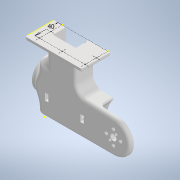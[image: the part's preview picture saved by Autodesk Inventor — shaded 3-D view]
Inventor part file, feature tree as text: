
AUTODESK INVENTOR PART (.ipt)
format: ipt  version: 2020 (Build 240168000, 168)  size: 836,608 bytes
history: native  units: mm
features: sketch x26, fillet x22, extrude x16, hole x7, other x6, reference x4, shell x1, projected_geometry x1
ambient origin geometry x8: Origin, YZ Plane, XZ Plane, XY Plane, X Axis, Y Axis, Z Axis, Center Point
bodies: Solid1 (feature_tree)
feature tree (83):
  extrude  "Extrusion1"  Depth=58.0mm
  shell  "Shell1"  Thickness=15.0mm
  extrude  "Extrusion2"  Depth=30.0mm
  extrude  "Extrusion3"  Depth=120.0mm
  hole  "Hole1"  [1 undecoded]
  extrude  "Extrusion5"  Depth=60.0mm
  hole  "Hole2"  [1 undecoded]
  extrude  "Extrusion6"  Depth=40.0mm
  extrude  "Extrusion7"  TaperAngle=0.0deg  [1 undecoded]
  extrude  "Extrusion8"  Depth=3.4mm
  fillet  "Fillet1"  Radius=6.3mm
  fillet  "Fillet2"  [1 undecoded]
  fillet  "Fillet4"  Radius=20.0mm
  fillet  "Fillet5"  Radius=81.0mm
  fillet  "Fillet7"  [1 undecoded]
  fillet  "Fillet10"  [1 undecoded]
  fillet  "Fillet11"  Radius=25.0mm
  fillet  "Fillet13"  Radius=3.4mm
  extrude  "Extrusion9"  TaperAngle=90.0deg  [1 undecoded]
  hole  "Hole3"  [1 undecoded]
  fillet  "Fillet15"  [1 undecoded]
  fillet  "Fillet16"  [1 undecoded]
  extrude  "Extrusion12"  Depth=90.0mm
  extrude  "Extrusion13"  Depth=12.0mm
  extrude  "Extrusion14"  Depth=24.0mm TaperAngle=0.0deg
  fillet  "Fillet17"  Radius=2.0mm
  fillet  "Fillet18"  Radius=18.0mm
  fillet  "Fillet19"  Radius=10.0mm
  fillet  "Fillet21"  Radius=18.0mm
  extrude  "Extrusion15"  Depth=4.0mm
  fillet  "Fillet24"  Radius=4.0mm
  fillet  "Fillet25"  Radius=7.0mm
  fillet  "Fillet26"  Radius=12.0mm
  fillet  "Fillet27"  Radius=5.5mm
  hole  "Hole6"  [1 undecoded]
  hole  "Hole7"  [1 undecoded]
  fillet  "Fillet28"  Radius=25.0mm
  sketch  "Sketch29"  dims[d114=5.0mm d115=3.0mm d116=0.0mm d117=25.0mm]
  extrude  "Extrusion16"  Depth=20.0mm TaperAngle=0.0deg
  hole  "Hole8"  [1 undecoded]
  extrude  "Extrusion17"  Depth=12.0mm
  extrude  "Extrusion18"  Depth=3.0mm
  hole  "Hole10"  [1 undecoded]
  extrude  "Extrusion19"  Depth=6.0mm TaperAngle=0.0deg
  fillet  "Fillet29"  Radius=10.0mm
  fillet  "Fillet30"  Radius=3.0mm
  sketch  "Sketch38"  dims[d146=3.0mm]
  sketch  "Sketch39"  dims[d147=3.4mm d148=15.875mm d149=11.0mm d150=2.6mm d151=90.0deg d152=8.0mm d153=0.0mm d154=40.0mm d155=3.4mm d156=15.875mm d157=6.3mm d158=2.6mm d159=90.0deg d160=8.0mm d161=0.0mm d162=3.0mm d163=4.0mm d164=2.0mm d165=0.0mm d166=2.4mm d167=5.0mm d168=4.4mm d169=2.0mm d170=90.0deg d171=5.0mm d172=20.594885mm d173=7.0mm d174=105.185mm d175=0.0mm d183=7.0mm d184=2.0mm d185=0.0mm d186=2.4mm d187=5.0mm d188=4.4mm d189=2.0mm d190=90.0deg d191=5.0mm d192=20.594885mm d193=4.0mm d194=4.5mm d195=0.0mm d196=5.0mm d197=4.0mm d199=7.0mm d200=7.0mm d216=5.0mm]
  fillet  "Fillet38"  Radius=3.0mm
  sketch  "Sketch1"  dims[d4=54.0mm d6=58.0mm d7=15.0mm]
  sketch  "Sketch3"  dims[d8=65.0mm d9=30.0mm]
  sketch  "Sketch4"  dims[d10=0.0mm d12=120.0mm]
  sketch  "Sketch5"  dims[d14=15.0mm d15=80.0mm]
  sketch  "Sketch7"  dims[d16=52.0mm d17=60.0mm]
  sketch  "Sketch8"  dims[d19=24.0mm d20=0.0mm]
  sketch  "Sketch9"  dims[d21=7.0mm d22=40.0mm]
  sketch  "Sketch10"  dims[d23=20.0mm d24=0.0mm]
  sketch  "Sketch11"  dims[d25=25.0mm d26=3.4mm d27=6.0mm d28=6.3mm d29=2.0mm d30=90.0deg d31=20.0mm d32=0.0mm d46=81.0mm d47=0.0mm d48=0.0mm d49=25.0mm d50=3.4mm d51=6.0mm]
  sketch  "Sketch13"  dims[d52=6.3mm d53=2.0mm d54=90.0deg]
  sketch  "Sketch16"  dims[d55=20.0mm d56=0.0mm d57=11.0mm d58=0.0mm d59=0.0mm]
  sketch  "Sketch20"  dims[d60=81.0mm d61=90.0mm]
  sketch  "Sketch22"  dims[d62=24.0mm d63=0.0mm d64=12.0mm]
  sketch  "Sketch23"  dims[d65=6.0mm d66=24.0mm d67=0.0mm d68=2.0mm d69=18.0mm d71=10.0mm d72=18.0mm]
  sketch  "Sketch24"  dims[d74=8.0mm d77=4.0mm d78=4.0mm d80=7.0mm d81=12.0mm d82=5.5mm]
  projected_geometry  "Projected Loop2"
  sketch  "Sketch26"  dims[d83=24.0mm d84=0.0mm]
  sketch  "Sketch28"  dims[d89=4.0mm d90=6.0mm d91=6.3mm d92=2.0mm d93=90.0deg d94=8.0mm d95=0.0mm d113=7.0mm]
  sketch  "Sketch30"  dims[d118=7.0mm d119=20.0mm d120=0.0mm]
  reference  "Reference1"
  reference  "Reference2"
  sketch  "Sketch31"  dims[d121=7.0mm d122=20.0mm]
  sketch  "Sketch32"  dims[d123=15.0mm d124=0.0mm d125=12.0mm]
  sketch  "Sketch33"  dims[d126=12.0mm d127=3.0mm]
  reference  "Reference3"
  reference  "Reference4"
  sketch  "Sketch36"  dims[d129=37.0mm d130=10.0mm]
  sketch  "Sketch37"  dims[d131=50.0mm d132=6.0mm d133=0.0mm d143=10.0mm d144=3.0mm d145=3.0mm]
  other  "<userpath>\Desktop\Robot_Project\Kang-BalancingRobot\Hardware\Cad\KangKang.iam"
  other  "KangKang.iam"
  other  "AS5147_ENC_ANGLE_VER01:1"
  other  "Board_86"
  other  "AS5147_ENC_VERTICAL_VER01:1"
  other  "Board_107"
note: 14 required parameter values undecoded (feature->parameter linkage not recoverable at this tier; creation-order binding heuristic only, values carry confidence <= 0.55)
